# Revit family: Ducto
name_source: partatom
category: Mechanical Equipment
units: mm (PartAtom-declared; Revit-internal decimal feet)

## family parameters
Always vertical = Yes
Classification = None
Cut with Voids When Loaded = No
Part Type = Normal
Room Calculation Point = No
Round Connector Dimension = Use Diameter
Shared = No
Work Plane-Based = No

## types (14) — shared parameters
00_20_Manufacturer = Blauberg
00_20_Name = Axial fans
Amperage = 0 A
Casing Material = Plastic, opaque, white
Description = For round channels
Frequency = 50 Hz
Load Classification = HVAC
Maintenance zone material = <By Category>
Manufacturer = Blauberg
N = 54 mm  [stored 0.177165 ft]
Number of Fase = 1
URL = https://blaubergventilatoren.de
Voltage = 230 V
zero-valued in all types: Default Elevation

## per-type parameters (varying)
| type | 00_20_Type | Apparent Load | D | Diameter | Dy | Dyv | Fastening | H | H1 | H2 | Height | K | K1 | K2 | L | L1 | L2 | Length | Maximum Air Flow | Power | Sound pressure level at 3 m distance | Weight | Width |
| Ducto 100 | Ducto  100 | 12 W | 100 mm  [stored 0.328084 ft] | 100 mm  [stored 0.328084 ft] | 96 mm  [stored 0.314961 ft] | 91 mm  [stored 0.298556 ft] | No | 109 mm  [stored 0.357612 ft] | 50 mm  [stored 0.164042 ft] | 54 mm  [stored 0.177165 ft] | 100 mm  [stored 0.328084 ft] | 159 mm  [stored 0.521654 ft] | 40 mm  [stored 0.131234 ft] | 141 mm | 138 mm  [stored 0.452756 ft] | 42 mm | 54 mm  [stored 0.177165 ft] | 138 mm  [stored 0.452756 ft] | 110.0 m³/h | 8 W | 25 dBA | 0.61 kg | 100 mm  [stored 0.328084 ft] |
| Ducto 125 | Ducto 125 | 21 W | 125 mm  [stored 0.410105 ft] | 125 mm  [stored 0.410105 ft] | 121 mm  [stored 0.396982 ft] | 116 mm  [stored 0.380577 ft] | No | 138 mm  [stored 0.452756 ft] | 63 mm | 71 mm | 125 mm  [stored 0.410105 ft] | 159 mm  [stored 0.521654 ft] | 40 mm  [stored 0.131234 ft] | 141 mm | 162 mm | 54 mm  [stored 0.177165 ft] | 66 mm | 162 mm | 215.0 m³/h | 13 W | 33 dBA | 0.75 kg | 125 mm  [stored 0.410105 ft] |
| Ducto 150 | Ducto 150 | 23 W | 150 mm | 150 mm | 146 mm  [stored 0.479003 ft] | 141 mm | No | 160 mm  [stored 0.524934 ft] | 75 mm | 80 mm  [stored 0.262467 ft] | 150 mm | 159 mm  [stored 0.521654 ft] | 40 mm  [stored 0.131234 ft] | 141 mm | 182 mm | 64 mm | 76 mm | 182 mm | 340.0 m³/h | 22 W | 39 dBA | 1.30 kg | 150 mm |
| Ducto-U 150 | Ducto-U 150 | 23 W | 150 mm | 150 mm | 146 mm  [stored 0.479003 ft] | 141 mm | Yes | 160 mm  [stored 0.524934 ft] | 75 mm | 80 mm  [stored 0.262467 ft] | 160 mm  [stored 0.524934 ft] | 190 mm | 48 mm  [stored 0.15748 ft] | 172 mm  [stored 0.564304 ft] | 182 mm | 64 mm | 76 mm | 182 mm | 340.0 m³/h | 22 W | 39 dBA | 1.30 kg | 190 mm |
| Ducto-U 100 | Ducto-U 100 | 12 W | 100 mm  [stored 0.328084 ft] | 100 mm  [stored 0.328084 ft] | 96 mm  [stored 0.314961 ft] | 91 mm  [stored 0.298556 ft] | Yes | 109 mm  [stored 0.357612 ft] | 50 mm  [stored 0.164042 ft] | 54 mm  [stored 0.177165 ft] | 109 mm  [stored 0.357612 ft] | 160 mm  [stored 0.524934 ft] | 40 mm  [stored 0.131234 ft] | 142 mm  [stored 0.465879 ft] | 138 mm  [stored 0.452756 ft] | 42 mm | 54 mm  [stored 0.177165 ft] | 138 mm  [stored 0.452756 ft] | 110.0 m³/h | 8 W | 25 dBA | 0.61 kg | 160 mm  [stored 0.524934 ft] |
| Ducto-U 125 | Ducto-U 125 | 21 W | 125 mm  [stored 0.410105 ft] | 125 mm  [stored 0.410105 ft] | 121 mm  [stored 0.396982 ft] | 116 mm  [stored 0.380577 ft] | Yes | 138 mm  [stored 0.452756 ft] | 63 mm | 71 mm | 138 mm  [stored 0.452756 ft] | 160 mm  [stored 0.524934 ft] | 40 mm  [stored 0.131234 ft] | 142 mm  [stored 0.465879 ft] | 162 mm | 54 mm  [stored 0.177165 ft] | 66 mm | 162 mm | 215.0 m³/h | 13 W | 33 dBA | 0.75 kg | 160 mm  [stored 0.524934 ft] |
| Ducto Plus 100 | Ducto Plus 100 | 12 W | 100 mm  [stored 0.328084 ft] | 100 mm  [stored 0.328084 ft] | 96 mm  [stored 0.314961 ft] | 91 mm  [stored 0.298556 ft] | No | 109 mm  [stored 0.357612 ft] | 50 mm  [stored 0.164042 ft] | 54 mm  [stored 0.177165 ft] | 100 mm  [stored 0.328084 ft] | 159 mm  [stored 0.521654 ft] | 40 mm  [stored 0.131234 ft] | 141 mm | 138 mm  [stored 0.452756 ft] | 42 mm | 54 mm  [stored 0.177165 ft] | 138 mm  [stored 0.452756 ft] | 110.0 m³/h | 8 W | 25 dBA | 0.61 kg | 100 mm  [stored 0.328084 ft] |
| Ducto Plus 125 | Ducto Plus 125 | 21 W | 125 mm  [stored 0.410105 ft] | 125 mm  [stored 0.410105 ft] | 121 mm  [stored 0.396982 ft] | 116 mm  [stored 0.380577 ft] | No | 138 mm  [stored 0.452756 ft] | 63 mm | 71 mm | 125 mm  [stored 0.410105 ft] | 159 mm  [stored 0.521654 ft] | 40 mm  [stored 0.131234 ft] | 141 mm | 162 mm | 54 mm  [stored 0.177165 ft] | 66 mm | 162 mm | 215.0 m³/h | 13 W | 33 dBA | 0.75 kg | 125 mm  [stored 0.410105 ft] |
| Ducto Plus 150 | Ducto Plus 150 | 23 W | 150 mm | 150 mm | 146 mm  [stored 0.479003 ft] | 141 mm | No | 160 mm  [stored 0.524934 ft] | 75 mm | 80 mm  [stored 0.262467 ft] | 150 mm | 159 mm  [stored 0.521654 ft] | 40 mm  [stored 0.131234 ft] | 141 mm | 182 mm | 64 mm | 76 mm | 182 mm | 340.0 m³/h | 22 W | 39 dBA | 1.30 kg | 150 mm |
| Ducto Power Plus 150 | Ducto Power Plus 150 | 25 W | 150 mm | 150 mm | 146 mm  [stored 0.479003 ft] | 141 mm | No | 160 mm  [stored 0.524934 ft] | 75 mm | 80 mm  [stored 0.262467 ft] | 150 mm | 159 mm  [stored 0.521654 ft] | 40 mm  [stored 0.131234 ft] | 141 mm | 182 mm | 64 mm | 76 mm | 182 mm | 375.0 m³/h | 25 W | 41 dBA | 1.30 kg | 150 mm |
| Ducto-U Plus 100 | Ducto-U Plus 100 | 12 W | 100 mm  [stored 0.328084 ft] | 100 mm  [stored 0.328084 ft] | 96 mm  [stored 0.314961 ft] | 91 mm  [stored 0.298556 ft] | Yes | 109 mm  [stored 0.357612 ft] | 50 mm  [stored 0.164042 ft] | 54 mm  [stored 0.177165 ft] | 109 mm  [stored 0.357612 ft] | 159 mm  [stored 0.521654 ft] | 40 mm  [stored 0.131234 ft] | 141 mm | 138 mm  [stored 0.452756 ft] | 42 mm | 54 mm  [stored 0.177165 ft] | 138 mm  [stored 0.452756 ft] | 110.0 m³/h | 8 W | 25 dBA | 0.61 kg | 159 mm  [stored 0.521654 ft] |
| Ducto-U Plus 125 | Ducto-U Plus 125 | 21 W | 125 mm  [stored 0.410105 ft] | 125 mm  [stored 0.410105 ft] | 121 mm  [stored 0.396982 ft] | 116 mm  [stored 0.380577 ft] | Yes | 138 mm  [stored 0.452756 ft] | 63 mm | 71 mm | 138 mm  [stored 0.452756 ft] | 159 mm  [stored 0.521654 ft] | 40 mm  [stored 0.131234 ft] | 141 mm | 162 mm | 54 mm  [stored 0.177165 ft] | 66 mm | 162 mm | 215.0 m³/h | 13 W | 33 dBA | 0.75 kg | 159 mm  [stored 0.521654 ft] |
| Ducto-U Plus 150 | Ducto-U Plus 150 | 23 W | 150 mm | 150 mm | 146 mm  [stored 0.479003 ft] | 141 mm | Yes | 160 mm  [stored 0.524934 ft] | 75 mm | 80 mm  [stored 0.262467 ft] | 160 mm  [stored 0.524934 ft] | 159 mm  [stored 0.521654 ft] | 40 mm  [stored 0.131234 ft] | 141 mm | 182 mm | 64 mm | 76 mm | 182 mm | 340.0 m³/h | 22 W | 39 dBA | 1.30 kg | 159 mm  [stored 0.521654 ft] |
| Ducto-U Power Plus 150 | Ducto-U Power Plus 150 | 25 W | 150 mm | 150 mm | 146 mm  [stored 0.479003 ft] | 141 mm | Yes | 160 mm  [stored 0.524934 ft] | 75 mm | 80 mm  [stored 0.262467 ft] | 160 mm  [stored 0.524934 ft] | 159 mm  [stored 0.521654 ft] | 40 mm  [stored 0.131234 ft] | 141 mm | 182 mm | 64 mm | 76 mm | 182 mm | 375.0 m³/h | 25 W | 41 dBA | 1.30 kg | 159 mm  [stored 0.521654 ft] |

note: [stored X ft] marks values corroborated as IEEE doubles in the binary element streams (Revit-internal decimal feet)
